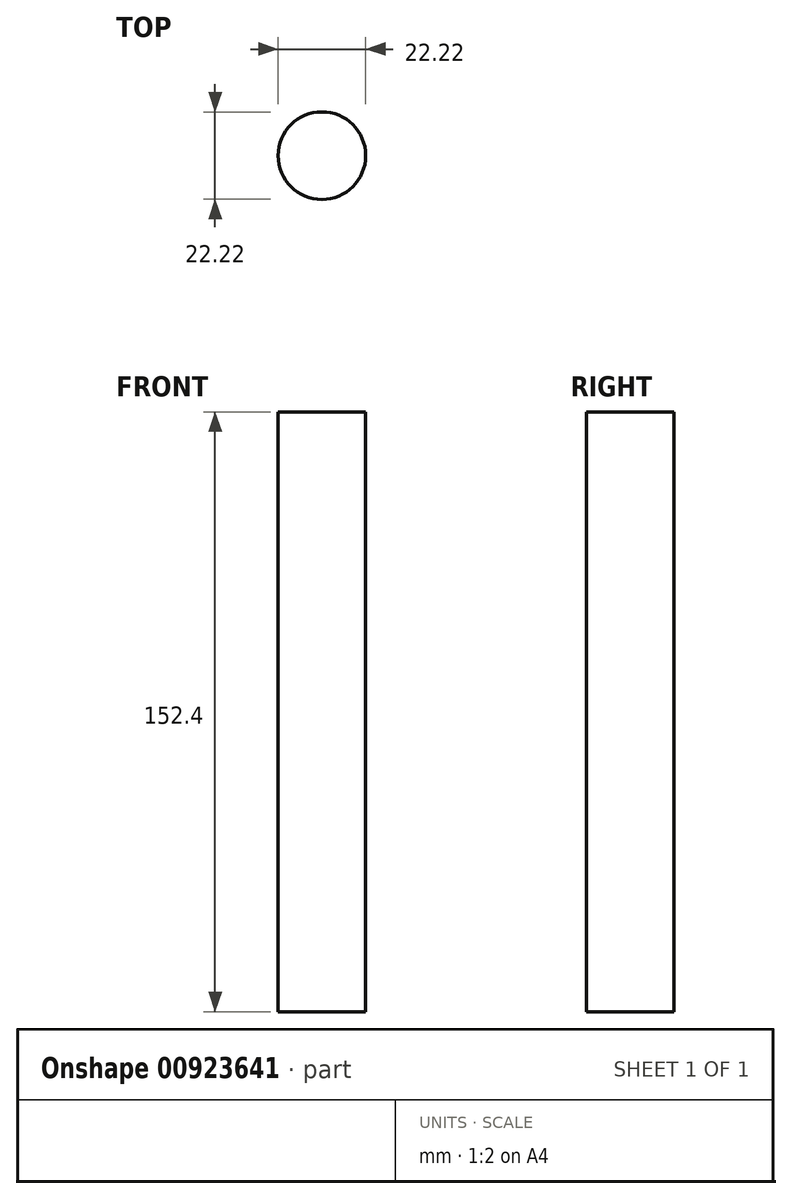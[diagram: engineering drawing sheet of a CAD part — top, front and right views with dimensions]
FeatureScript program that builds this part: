
annotation { "Feature Type Name" : "Feature", "Feature Type Description" : "" }
export const myFeature = defineFeature(function(context is Context, id is Id, definition is map)
    precondition{}
    {
        {
            var Q0;
            Q0=qCreatedBy(makeId("Top.planeOp"),FACE);
            var sketch = newSketch(context, id + "F0", { "sketchPlane" : qUnion([Q0])});
            skCircle(sketch, "E0", {"center": v(0, 0) * mm, "radius": 11.11 * mm});
            skSolve(sketch);
        }
        {
            var Q0;
            Q0=qSketchRegion(id+"F0",true);
            extrude(context, id + "F1", {"entities" : qUnion([Q0]), "depth" : 152.4 * mm});
        }
    });
